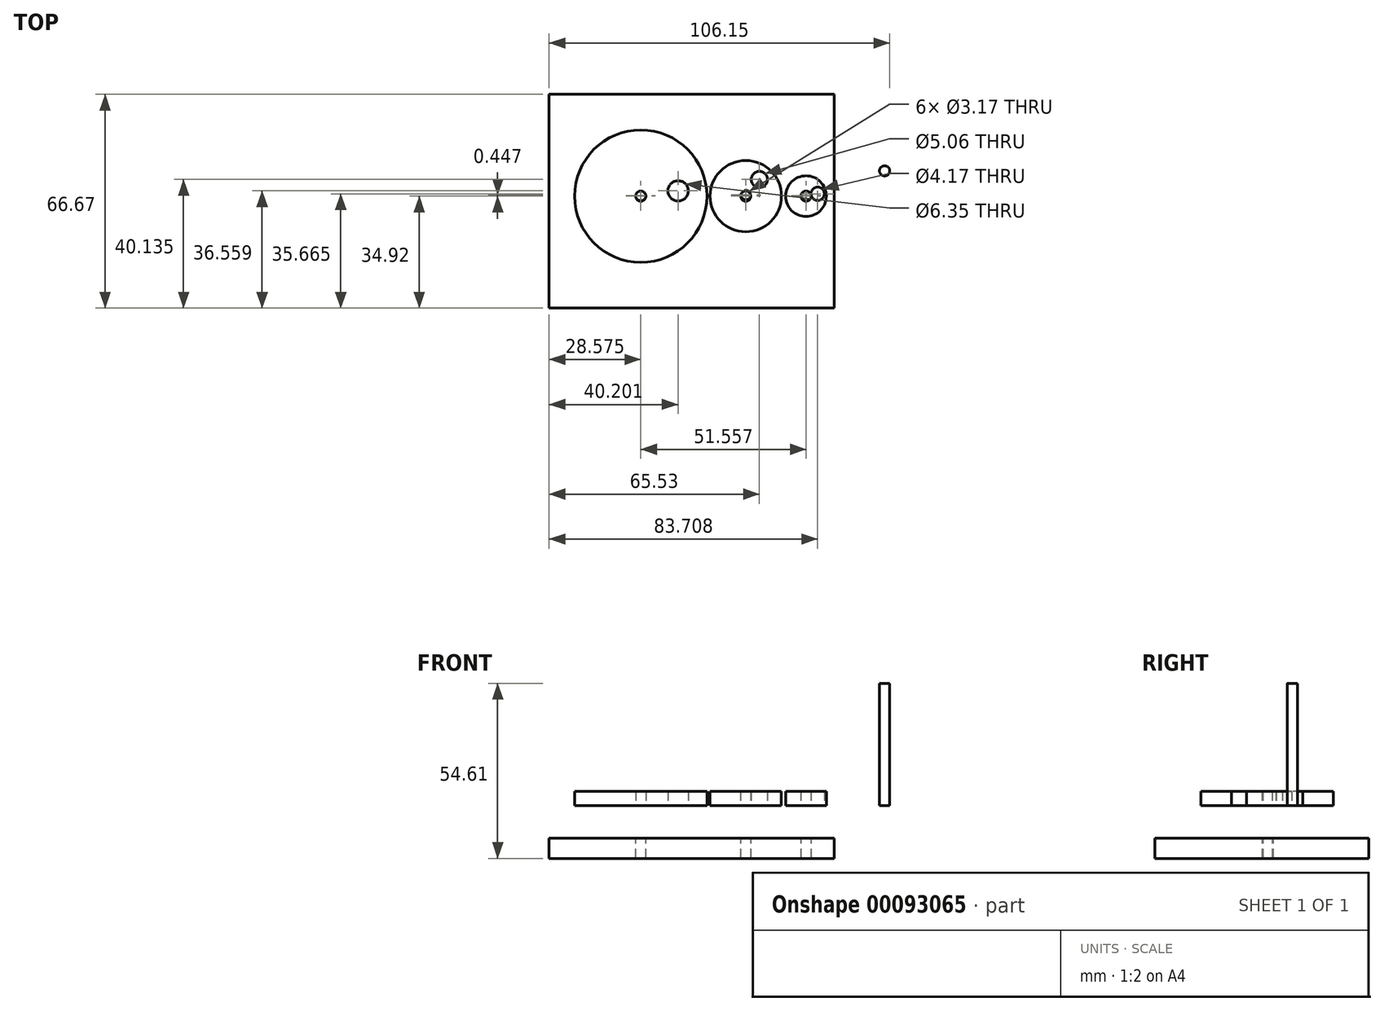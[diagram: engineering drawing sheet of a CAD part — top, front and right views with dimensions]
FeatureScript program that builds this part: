
annotation { "Feature Type Name" : "Feature", "Feature Type Description" : "" }
export const myFeature = defineFeature(function(context is Context, id is Id, definition is map)
    precondition{}
    {
        {
            var Q0;
            Q0=qCreatedBy(makeId("Top.planeOp"),FACE);
            var sketch = newSketch(context, id + "F0", { "sketchPlane" : qUnion([Q0])});
            skCircle(sketch, "E0", {"center": v(-45.9, 0) * mm, "radius": 20.64 * mm});
            skCircle(sketch, "E1", {"center": v(-13.17, 0) * mm, "radius": 11.11 * mm});
            skCircle(sketch, "E2", {"center": v(5.6, 0) * mm, "radius": 6.35 * mm});
            skCircle(sketch, "E3", {"center": v(-45.9, 0) * mm, "radius": 1.59 * mm});
            skCircle(sketch, "E4", {"center": v(-13.17, 0) * mm, "radius": 1.59 * mm});
            skCircle(sketch, "E5", {"center": v(5.6, 0) * mm, "radius": 1.59 * mm});
            skCircle(sketch, "E6", {"center": v(-34.27, 1.64) * mm, "radius": 3.18 * mm});
            skCircle(sketch, "E7", {"center": v(-8.94, 5.21) * mm, "radius": 2.53 * mm});
            skCircle(sketch, "E8", {"center": v(9.24, 0.74) * mm, "radius": 2.09 * mm});
            skSolve(sketch);
        }
        {
            var Q0;
            Q0=qCreatedBy(makeId("Top.planeOp"),FACE);
            var sketch = newSketch(context, id + "F1", { "sketchPlane" : qUnion([Q0])});
            skLineSegment(sketch, "E9.bottom", {"start": v(-74.47, 31.75) * mm, "end": v(14.43, 31.75) * mm});
            skLineSegment(sketch, "E9.top", {"start": v(-74.47, -34.92) * mm, "end": v(14.43, -34.92) * mm});
            skLineSegment(sketch, "E9.left", {"start": v(-74.47, 31.75) * mm, "end": v(-74.47, -34.92) * mm});
            skLineSegment(sketch, "E9.right", {"start": v(14.43, 31.75) * mm, "end": v(14.43, -34.92) * mm});
            skCircle(sketch, "E10", {"center": v(-45.9, 0.15) * mm, "radius": 1.59 * mm});
            skCircle(sketch, "E11", {"center": v(-13.11, 0.45) * mm, "radius": 1.59 * mm});
            skCircle(sketch, "E12", {"center": v(5.66, 0.15) * mm, "radius": 1.59 * mm});
            skSolve(sketch);
        }
        {
            var Q0;
            Q0=qCreatedBy(makeId("Top.planeOp"),FACE);
            var sketch = newSketch(context, id + "F2", { "sketchPlane" : qUnion([Q0])});
            skCircle(sketch, "E13", {"center": v(30.1, 7.9) * mm, "radius": 1.59 * mm});
            skSolve(sketch);
        }
        {
            var Q0;
            Q0 = qSketchRegion(id + "F1", true);
            extrude(context, id + "F3", {"entities" : qUnion([Q0]), "oppositeDirection" : true, "depth" : 16.5 * mm});
        }
        {
            var Q0;
            Q0 = qSketchRegion(id + "F1", true);
            extrude(context, id + "F4", {"entities" : qUnion([Q0]), "operationType" : NewBodyOperationType.REMOVE, "oppositeDirection" : true, "depth" : 10.16 * mm});
        }
        {
            var Q0;
            Q0 = qSketchRegion(id + "F0", true);
            extrude(context, id + "F5", {"entities" : qUnion([Q0]), "depth" : 4.44 * mm});
        }
        {
            var Q0;
            Q0=makeQuery(id+"F2.imprint","IMPRINT",FACE,{"disambiguationData":[TD([[makeQuery(id+"F2.imprint","IMPRINT",EDGE,{"derivedFrom":sQuery(id+"F2.wireOp",EDGE,"E13")}),1.0]])]});
            extrude(context, id + "F6", {"entities" : qUnion([Q0]), "depth" : 38.1 * mm});
        }
    });
